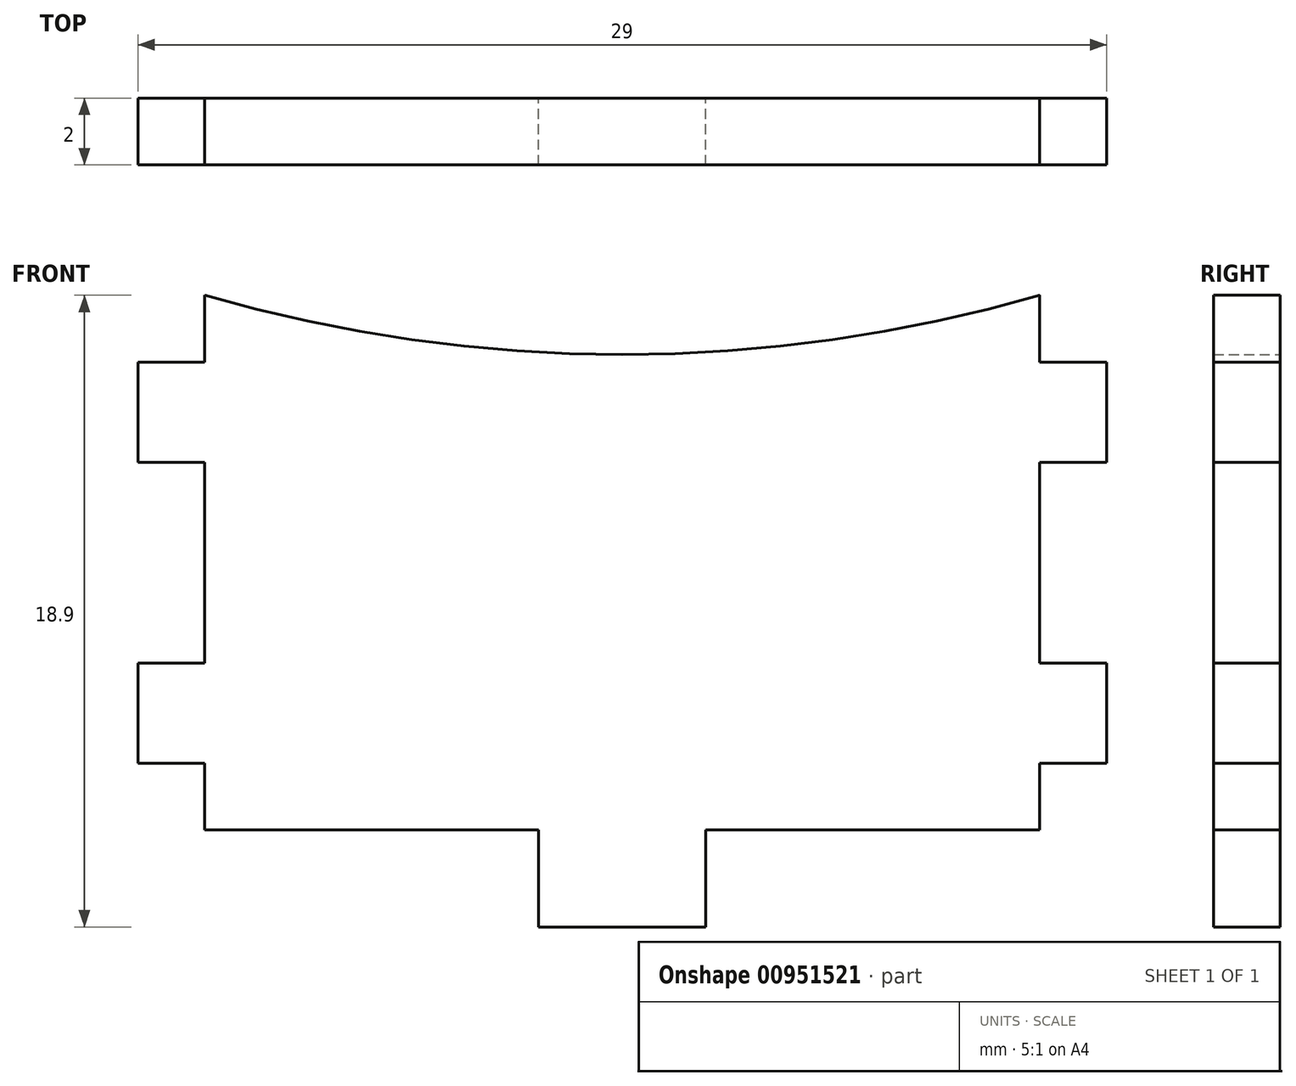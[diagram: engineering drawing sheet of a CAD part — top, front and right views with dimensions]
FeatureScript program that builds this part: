
annotation { "Feature Type Name" : "Feature", "Feature Type Description" : "" }
export const myFeature = defineFeature(function(context is Context, id is Id, definition is map)
    precondition{}
    {
        {
            var Q0;
            Q0=qCreatedBy(makeId("Front.planeOp"),FACE);
            var sketch = newSketch(context, id + "F0", { "sketchPlane" : qUnion([Q0])});
            skLineSegment(sketch, "E0", {"start": v(0, 0) * mm, "end": v(25, 0) * mm});
            skLineSegment(sketch, "E1", {"start": v(25, 0) * mm, "end": v(25, 2) * mm});
            skLineSegment(sketch, "E2", {"start": v(0, 0) * mm, "end": v(0, 2) * mm});
            skLineSegment(sketch, "E3", {"start": v(10, 0) * mm, "end": v(10, -2.9) * mm});
            skLineSegment(sketch, "E4", {"start": v(10, -2.9) * mm, "end": v(15, -2.9) * mm});
            skLineSegment(sketch, "E5", {"start": v(15, -2.9) * mm, "end": v(15, 0) * mm});
            skLineSegment(sketch, "E6", {"start": v(-2, 2) * mm, "end": v(0, 2) * mm});
            skLineSegment(sketch, "E7", {"start": v(-2, 2) * mm, "end": v(-2, 5) * mm});
            skLineSegment(sketch, "E8", {"start": v(0, 5) * mm, "end": v(-2, 5) * mm});
            skLineSegment(sketch, "E9", {"start": v(0, 5) * mm, "end": v(0, 11) * mm});
            skLineSegment(sketch, "E10", {"start": v(-2, 11) * mm, "end": v(0, 11) * mm});
            skLineSegment(sketch, "E11", {"start": v(-2, 11) * mm, "end": v(-2, 14) * mm});
            skLineSegment(sketch, "E12", {"start": v(0, 14) * mm, "end": v(-2, 14) * mm});
            skLineSegment(sketch, "E13", {"start": v(0, 14) * mm, "end": v(0, 16) * mm});
            skLineSegment(sketch, "E14", {"start": v(27, 2) * mm, "end": v(25, 2) * mm});
            skLineSegment(sketch, "E15", {"start": v(27, 2) * mm, "end": v(27, 5) * mm});
            skLineSegment(sketch, "E16", {"start": v(25, 5) * mm, "end": v(27, 5) * mm});
            skLineSegment(sketch, "E17", {"start": v(25, 5) * mm, "end": v(25, 11) * mm});
            skLineSegment(sketch, "E18", {"start": v(27, 11) * mm, "end": v(25, 11) * mm});
            skLineSegment(sketch, "E19", {"start": v(27, 11) * mm, "end": v(27, 14) * mm});
            skLineSegment(sketch, "E20", {"start": v(25, 14) * mm, "end": v(27, 14) * mm});
            skLineSegment(sketch, "E21", {"start": v(25, 14) * mm, "end": v(25, 16) * mm});
            skArc(sketch, "E22", {"start": v(0, 16) * mm, "mid": v(12.5, 14.23) * mm, "end": v(25, 16) * mm});
            skSolve(sketch);
        }
        {
            var Q0;
            Q0 = qSketchRegion(id + "F0", true);
            extrude(context, id + "F1", {"entities" : qUnion([Q0]), "depth" : 2 * mm, "offsetDistance" : 25 * mm});
        }
    });
